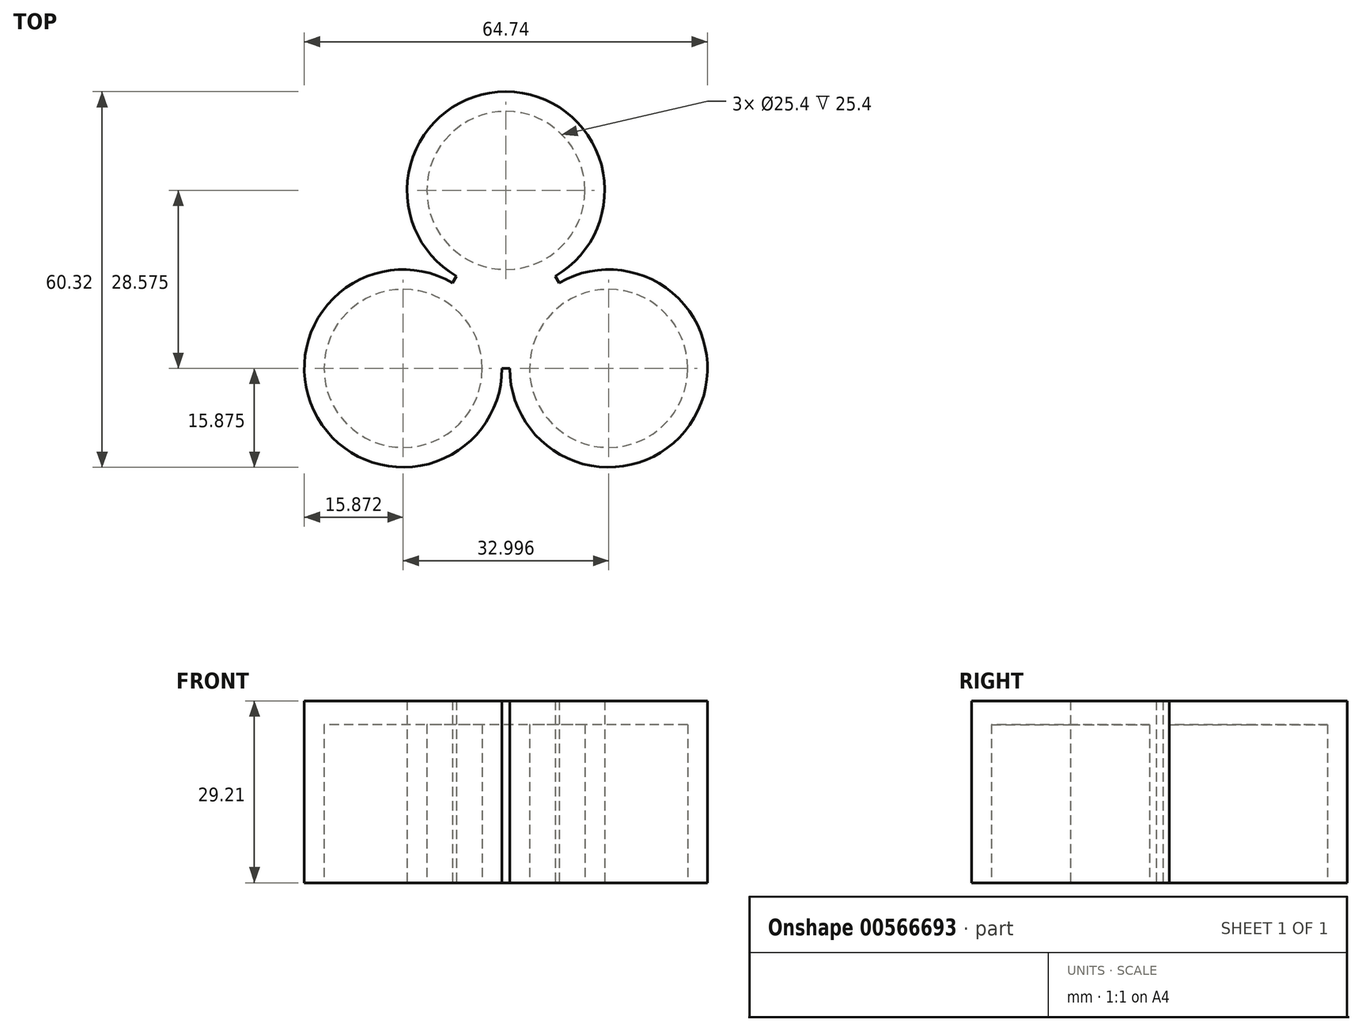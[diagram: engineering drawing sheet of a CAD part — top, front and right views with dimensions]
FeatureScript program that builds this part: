
annotation { "Feature Type Name" : "Feature", "Feature Type Description" : "" }
export const myFeature = defineFeature(function(context is Context, id is Id, definition is map)
    precondition{}
    {
        {
            var Q0;
            Q0=qCreatedBy(makeId("Top.planeOp"),FACE);
            var sketch = newSketch(context, id + "F0", { "sketchPlane" : qUnion([Q0])});
            skLineSegment(sketch, "E0", {"start": v(0, 0) * mm, "end": v(-16.5, -9.53) * mm});
            skLineSegment(sketch, "E1", {"start": v(0, 0) * mm, "end": v(16.5, -9.52) * mm});
            skLineSegment(sketch, "E2", {"start": v(0, 0) * mm, "end": v(0, 19.05) * mm});
            skCircle(sketch, "E3", {"center": v(-16.5, -9.53) * mm, "radius": 12.7 * mm});
            skCircle(sketch, "E4", {"center": v(0, 19.05) * mm, "radius": 15.88 * mm});
            skCircle(sketch, "E5", {"center": v(16.5, -9.52) * mm, "radius": 12.7 * mm});
            skCircle(sketch, "E6", {"center": v(-16.5, -9.53) * mm, "radius": 15.88 * mm});
            skCircle(sketch, "E7", {"center": v(0, 19.05) * mm, "radius": 12.7 * mm});
            skCircle(sketch, "E8", {"center": v(16.5, -9.52) * mm, "radius": 15.88 * mm});
            skLineSegment(sketch, "E9", {"start": v(-16.5, -9.53) * mm, "end": v(16.5, -9.52) * mm});
            skLineSegment(sketch, "E10", {"start": v(0, 19.05) * mm, "end": v(-16.5, -9.53) * mm});
            skLineSegment(sketch, "E11", {"start": v(0, 19.05) * mm, "end": v(16.5, -9.52) * mm});
            skSolve(sketch);
        }
        {
            var Q0;
            Q0=makeQuery(id+"F0.imprint","IMPRINT",FACE,{"disambiguationData":[TD([[makeQuery(id+"F0.imprint","IMPRINT",EDGE,{"derivedFrom":sQuery(id+"F0.wireOp",EDGE,"E3")}),-1.0]])]});
            var Q1;
            Q1=makeQuery(id+"F0.imprint","IMPRINT",FACE,{"disambiguationData":[TD([[makeQuery(id+"F0.imprint","IMPRINT",EDGE,{"derivedFrom":sQuery(id+"F0.wireOp",EDGE,"E5")}),-1.0]])]});
            var Q2;
            Q2=makeQuery(id+"F0.imprint","IMPRINT",FACE,{"disambiguationData":[TD([[makeQuery(id+"F0.imprint","IMPRINT",EDGE,{"derivedFrom":sQuery(id+"F0.wireOp",EDGE,"E4")}),1.0]])]});
            var Q3;
            {var subQ0=sQuery(id+"F0.wireOp",EDGE,"E10");var subQ5=sQuery(id+"F0.wireOp",EDGE,"E4");var subQ6=makeQuery(id+"F0.imprint","INTERSECT",VERTEX,{"derivedFrom":[subQ5,subQ0]});Q3=makeQuery(id+"F0.imprint","IMPRINT",FACE,{"disambiguationData":[TD([[makeQuery(id+"F0.imprint","IMPRINT",EDGE,{"disambiguationData":[TD([[subQ6,-1.0]])],"derivedFrom":subQ5}),-1.0]])]});}
            var Q4;
            {var subQ0=sQuery(id+"F0.wireOp",EDGE,"E11");var subQ5=sQuery(id+"F0.wireOp",EDGE,"E4");var subQ6=makeQuery(id+"F0.imprint","INTERSECT",VERTEX,{"derivedFrom":[subQ5,subQ0]});Q4=makeQuery(id+"F0.imprint","IMPRINT",FACE,{"disambiguationData":[TD([[makeQuery(id+"F0.imprint","IMPRINT",EDGE,{"disambiguationData":[TD([[subQ6,1.0]])],"derivedFrom":subQ5}),-1.0]])]});}
            var Q5;
            {var subQ0=sQuery(id+"F0.wireOp",EDGE,"E9");var subQ1=sQuery(id+"F0.wireOp",EDGE,"E6");var subQ2=makeQuery(id+"F0.imprint","INTERSECT",VERTEX,{"derivedFrom":[subQ1,subQ0]});Q5=makeQuery(id+"F0.imprint","IMPRINT",FACE,{"disambiguationData":[TD([[makeQuery(id+"F0.imprint","IMPRINT",EDGE,{"disambiguationData":[TD([[subQ2,-1.0]])],"derivedFrom":subQ1}),-1.0]])]});}
            extrude(context, id + "F1", {"entities" : qUnion([Q0, Q1, Q2, Q3, Q4, Q5]), "depth" : 25.4 * mm, "offsetDistance" : 25.4 * mm});
        }
        {
            var Q0;
            Q0=makeQuery(id+"F1.opExtrude","CAP_FACE",FACE,{"disambiguationData":[OSD([sQuery(id+"F0.wireOp",EDGE,"E3"),sQuery(id+"F0.wireOp",EDGE,"E4"),sQuery(id+"F0.wireOp",EDGE,"E5"),sQuery(id+"F0.wireOp",EDGE,"E6"),sQuery(id+"F0.wireOp",EDGE,"E7"),sQuery(id+"F0.wireOp",EDGE,"E8"),sQuery(id+"F0.wireOp",EDGE,"E9"),sQuery(id+"F0.wireOp",EDGE,"E10"),sQuery(id+"F0.wireOp",EDGE,"E11")])],"isStart":false});
            var sketch = newSketch(context, id + "F2", { "sketchPlane" : qUnion([Q0])});
            skLineSegment(sketch, "E12.0.0", {"start": v(-7.94, 5.3) * mm, "end": v(-8.56, 4.22) * mm});
            skArc(sketch, "E12.0.1", {"start": v(-8.56, 4.22) * mm, "mid": v(-30.25, -17.46) * mm, "end": v(-0.62, -9.53) * mm});
            skLineSegment(sketch, "E12.0.2", {"start": v(-0.62, -9.53) * mm, "end": v(0.62, -9.53) * mm});
            skArc(sketch, "E12.0.3", {"start": v(0.62, -9.52) * mm, "mid": v(30.25, -17.46) * mm, "end": v(8.56, 4.22) * mm});
            skLineSegment(sketch, "E12.0.4", {"start": v(8.56, 4.22) * mm, "end": v(7.94, 5.3) * mm});
            skArc(sketch, "E12.0.5", {"start": v(7.94, 5.3) * mm, "mid": v(0, 34.92) * mm, "end": v(-7.94, 5.3) * mm});
            skSolve(sketch);
        }
        {
            var Q0;
            Q0=makeQuery(id+"F2.imprint","IMPRINT",FACE,{"disambiguationData":[TD([[makeQuery(id+"F2.imprint","IMPRINT",EDGE,{"derivedFrom":sQuery(id+"F2.wireOp",EDGE,"E12.0.0")}),1.0]])]});
            var Q1;
            Q1=makeQuery(id+"F2.imprint","IMPRINT",FACE,{"disambiguationData":[TD([[makeQuery(id+"F2.imprint","IMPRINT",EDGE,{"derivedFrom":makeQuery(id+"F1.opExtrude","CAP_EDGE",EDGE,{"disambiguationData":[OSD([sQuery(id+"F0.wireOp",EDGE,"E3")])],"isStart":false})}),1.0]])]});
            var Q2;
            Q2=makeQuery(id+"F2.imprint","IMPRINT",FACE,{"disambiguationData":[TD([[makeQuery(id+"F2.imprint","IMPRINT",EDGE,{"derivedFrom":makeQuery(id+"F1.opExtrude","CAP_EDGE",EDGE,{"disambiguationData":[OSD([sQuery(id+"F0.wireOp",EDGE,"E5")])],"isStart":false})}),1.0]])]});
            var Q3;
            Q3=makeQuery(id+"F2.imprint","IMPRINT",FACE,{"disambiguationData":[TD([[makeQuery(id+"F2.imprint","IMPRINT",EDGE,{"derivedFrom":makeQuery(id+"F1.opExtrude","CAP_EDGE",EDGE,{"disambiguationData":[OSD([sQuery(id+"F0.wireOp",EDGE,"E7")])],"isStart":false})}),1.0]])]});
            extrude(context, id + "F3", {"entities" : qUnion([Q0, Q1, Q2, Q3]), "operationType" : NewBodyOperationType.ADD, "depth" : 3.8 * mm, "offsetDistance" : 25.4 * mm});
        }
    });
